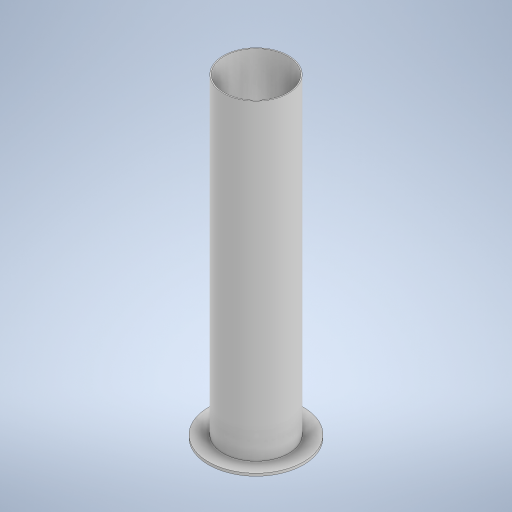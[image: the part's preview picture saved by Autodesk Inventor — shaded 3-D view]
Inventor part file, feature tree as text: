
AUTODESK INVENTOR PART (.ipt)
format: ipt  version: 2024 (Build 280153000, 153)  size: 242,688 bytes
history: native  units: mm
features: extrude x2, sketch x2, other x1
ambient origin geometry x8: Origin, YZ Plane, XZ Plane, XY Plane, X Axis, Y Axis, Z Axis, Center Point
bodies: Body1 (feature_tree)
feature tree (5):
  other  "Sólido1"
  extrude  "Extrusión1"  Depth=193.6mm
  extrude  "Extrusión2"  Depth=8.0mm
  sketch  "Boceto1"  dims[d0=200.0mm d1=193.6mm]
  sketch  "Boceto2"  dims[d2=955.0mm d3=0.0mm d4=290.0mm d5=8.0mm d6=0.0mm]
